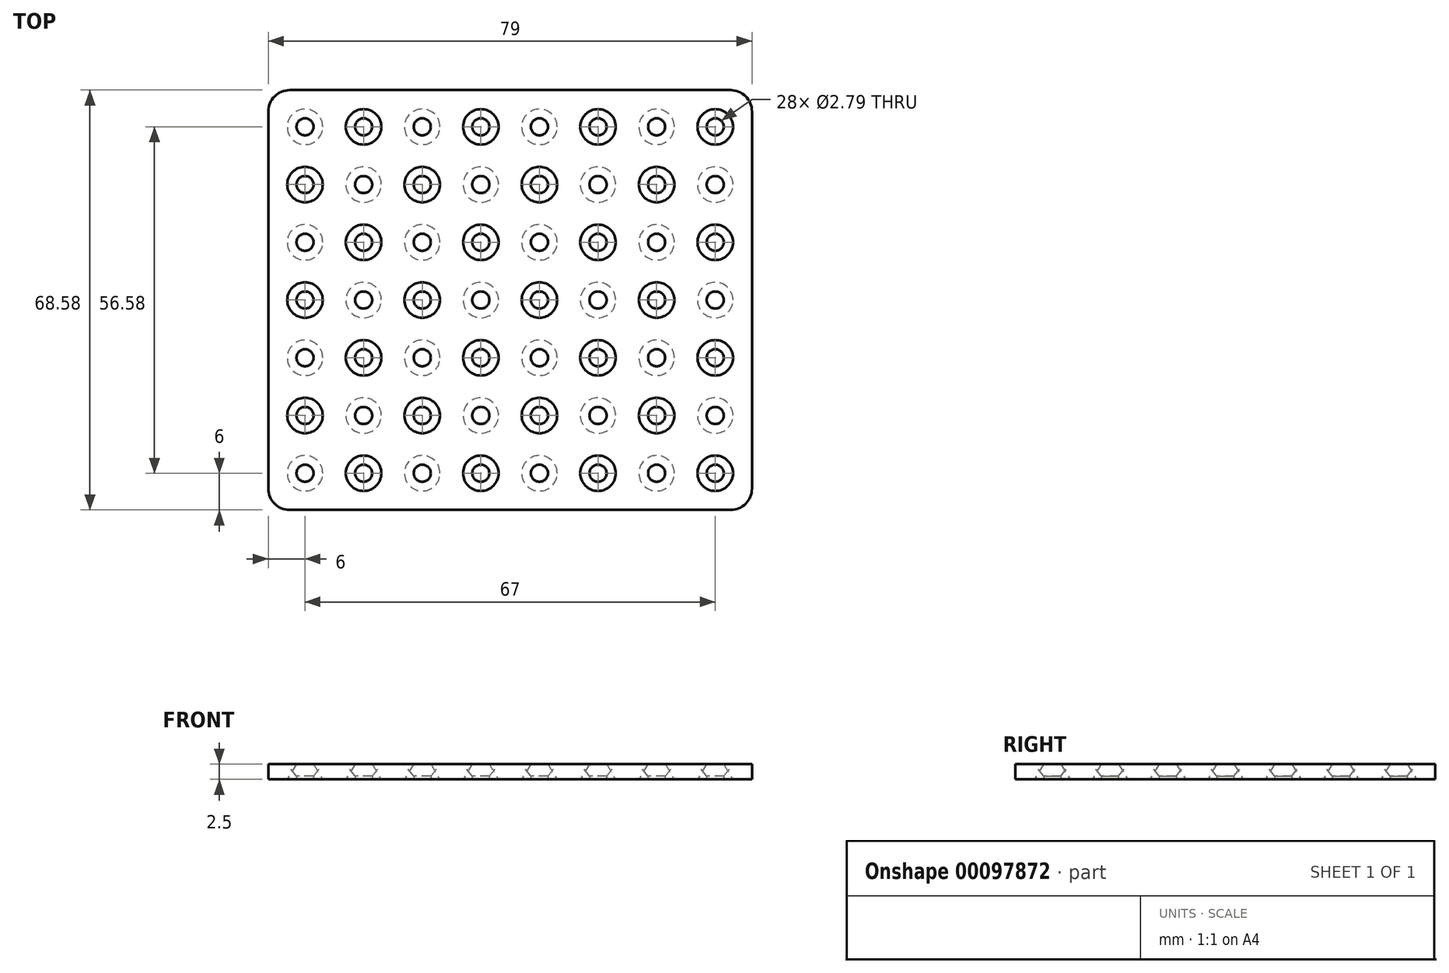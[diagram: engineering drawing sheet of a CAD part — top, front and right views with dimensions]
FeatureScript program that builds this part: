
annotation { "Feature Type Name" : "Feature", "Feature Type Description" : "" }
export const myFeature = defineFeature(function(context is Context, id is Id, definition is map)
    precondition{}
    {
        {
            var Q0;
            Q0=qCreatedBy(makeId("Top.planeOp"),FACE);
            var sketch = newSketch(context, id + "F0", { "sketchPlane" : qUnion([Q0])});
            skLineSegment(sketch, "E0.rect.bottom", {"start": v(39.5, 34.3) * mm, "end": v(-39.5, 34.3) * mm});
            skLineSegment(sketch, "E0.rect.top", {"start": v(39.5, -34.3) * mm, "end": v(-39.5, -34.3) * mm});
            skLineSegment(sketch, "E0.rect.left", {"start": v(39.5, 34.3) * mm, "end": v(39.5, -34.3) * mm});
            skLineSegment(sketch, "E0.rect.right", {"start": v(-39.5, 34.3) * mm, "end": v(-39.5, -34.3) * mm});
            skPoint(sketch, "E0.rect.middle", {"position": v(0, 0) * mm});
            skCircle(sketch, "E1", {"center": v(33.5, 28.3) * mm, "radius": 1.4 * mm});
            skCircle(sketch, "E2.0.1.0", {"center": v(33.5, 18.86) * mm, "radius": 1.4 * mm});
            skCircle(sketch, "E2.0.2.0", {"center": v(33.5, 9.43) * mm, "radius": 1.4 * mm});
            skCircle(sketch, "E2.0.3.0", {"center": v(33.5, 0) * mm, "radius": 1.4 * mm});
            skCircle(sketch, "E2.0.4.0", {"center": v(33.5, -9.43) * mm, "radius": 1.4 * mm});
            skCircle(sketch, "E2.0.5.0", {"center": v(33.5, -18.86) * mm, "radius": 1.4 * mm});
            skCircle(sketch, "E2.0.6.0", {"center": v(33.5, -28.3) * mm, "radius": 1.4 * mm});
            skCircle(sketch, "E2.1.0.0", {"center": v(23.93, 28.3) * mm, "radius": 1.4 * mm});
            skCircle(sketch, "E2.1.1.0", {"center": v(23.93, 18.86) * mm, "radius": 1.4 * mm});
            skCircle(sketch, "E2.1.2.0", {"center": v(23.93, 9.43) * mm, "radius": 1.4 * mm});
            skCircle(sketch, "E2.1.3.0", {"center": v(23.93, 0) * mm, "radius": 1.4 * mm});
            skCircle(sketch, "E2.1.4.0", {"center": v(23.93, -9.43) * mm, "radius": 1.4 * mm});
            skCircle(sketch, "E2.1.5.0", {"center": v(23.93, -18.86) * mm, "radius": 1.4 * mm});
            skCircle(sketch, "E2.1.6.0", {"center": v(23.93, -28.3) * mm, "radius": 1.4 * mm});
            skCircle(sketch, "E2.2.0.0", {"center": v(14.36, 28.3) * mm, "radius": 1.4 * mm});
            skCircle(sketch, "E2.2.1.0", {"center": v(14.36, 18.86) * mm, "radius": 1.4 * mm});
            skCircle(sketch, "E2.2.2.0", {"center": v(14.36, 9.43) * mm, "radius": 1.4 * mm});
            skCircle(sketch, "E2.2.3.0", {"center": v(14.36, 0) * mm, "radius": 1.4 * mm});
            skCircle(sketch, "E2.2.4.0", {"center": v(14.36, -9.43) * mm, "radius": 1.4 * mm});
            skCircle(sketch, "E2.2.5.0", {"center": v(14.36, -18.86) * mm, "radius": 1.4 * mm});
            skCircle(sketch, "E2.2.6.0", {"center": v(14.36, -28.3) * mm, "radius": 1.4 * mm});
            skCircle(sketch, "E2.3.0.0", {"center": v(4.79, 28.3) * mm, "radius": 1.4 * mm});
            skCircle(sketch, "E2.3.1.0", {"center": v(4.79, 18.86) * mm, "radius": 1.4 * mm});
            skCircle(sketch, "E2.3.2.0", {"center": v(4.79, 9.43) * mm, "radius": 1.4 * mm});
            skCircle(sketch, "E2.3.3.0", {"center": v(4.79, 0) * mm, "radius": 1.4 * mm});
            skCircle(sketch, "E2.3.4.0", {"center": v(4.79, -9.43) * mm, "radius": 1.4 * mm});
            skCircle(sketch, "E2.3.5.0", {"center": v(4.79, -18.86) * mm, "radius": 1.4 * mm});
            skCircle(sketch, "E2.3.6.0", {"center": v(4.79, -28.3) * mm, "radius": 1.4 * mm});
            skCircle(sketch, "E2.4.0.0", {"center": v(-4.79, 28.3) * mm, "radius": 1.4 * mm});
            skCircle(sketch, "E2.4.1.0", {"center": v(-4.79, 18.86) * mm, "radius": 1.4 * mm});
            skCircle(sketch, "E2.4.2.0", {"center": v(-4.79, 9.43) * mm, "radius": 1.4 * mm});
            skCircle(sketch, "E2.4.3.0", {"center": v(-4.79, 0) * mm, "radius": 1.4 * mm});
            skCircle(sketch, "E2.4.4.0", {"center": v(-4.79, -9.43) * mm, "radius": 1.4 * mm});
            skCircle(sketch, "E2.4.5.0", {"center": v(-4.79, -18.86) * mm, "radius": 1.4 * mm});
            skCircle(sketch, "E2.4.6.0", {"center": v(-4.79, -28.3) * mm, "radius": 1.4 * mm});
            skCircle(sketch, "E2.5.0.0", {"center": v(-14.36, 28.3) * mm, "radius": 1.4 * mm});
            skCircle(sketch, "E2.5.1.0", {"center": v(-14.36, 18.86) * mm, "radius": 1.4 * mm});
            skCircle(sketch, "E2.5.2.0", {"center": v(-14.36, 9.43) * mm, "radius": 1.4 * mm});
            skCircle(sketch, "E2.5.3.0", {"center": v(-14.36, 0) * mm, "radius": 1.4 * mm});
            skCircle(sketch, "E2.5.4.0", {"center": v(-14.36, -9.43) * mm, "radius": 1.4 * mm});
            skCircle(sketch, "E2.5.5.0", {"center": v(-14.36, -18.86) * mm, "radius": 1.4 * mm});
            skCircle(sketch, "E2.5.6.0", {"center": v(-14.36, -28.3) * mm, "radius": 1.4 * mm});
            skCircle(sketch, "E2.6.0.0", {"center": v(-23.93, 28.3) * mm, "radius": 1.4 * mm});
            skCircle(sketch, "E2.6.1.0", {"center": v(-23.93, 18.86) * mm, "radius": 1.4 * mm});
            skCircle(sketch, "E2.6.2.0", {"center": v(-23.93, 9.43) * mm, "radius": 1.4 * mm});
            skCircle(sketch, "E2.6.3.0", {"center": v(-23.93, 0) * mm, "radius": 1.4 * mm});
            skCircle(sketch, "E2.6.4.0", {"center": v(-23.93, -9.43) * mm, "radius": 1.4 * mm});
            skCircle(sketch, "E2.6.5.0", {"center": v(-23.93, -18.86) * mm, "radius": 1.4 * mm});
            skCircle(sketch, "E2.6.6.0", {"center": v(-23.93, -28.3) * mm, "radius": 1.4 * mm});
            skLineSegment(sketch, "E2.direction1", {"start": v(33.5, 28.3) * mm, "end": v(23.93, 28.3) * mm, "construction": true});
            skLineSegment(sketch, "E2.direction2", {"start": v(33.5, 28.3) * mm, "end": v(33.5, 18.86) * mm, "construction": true});
            skCircle(sketch, "E3.0.7.0", {"center": v(-33.5, 28.3) * mm, "radius": 1.4 * mm});
            skCircle(sketch, "E3.0.7.1", {"center": v(-33.5, 18.86) * mm, "radius": 1.4 * mm});
            skCircle(sketch, "E3.0.7.2", {"center": v(-33.5, 9.43) * mm, "radius": 1.4 * mm});
            skCircle(sketch, "E3.0.7.3", {"center": v(-33.5, 0) * mm, "radius": 1.4 * mm});
            skCircle(sketch, "E3.0.7.4", {"center": v(-33.5, -9.43) * mm, "radius": 1.4 * mm});
            skCircle(sketch, "E3.0.7.5", {"center": v(-33.5, -18.86) * mm, "radius": 1.4 * mm});
            skCircle(sketch, "E3.0.7.6", {"center": v(-33.5, -28.3) * mm, "radius": 1.4 * mm});
            skSolve(sketch);
        }
        {
            var Q0;
            Q0=makeQuery(id+"F0.imprint","IMPRINT",FACE,{"disambiguationData":[TD([[makeQuery(id+"F0.imprint","IMPRINT",EDGE,{"derivedFrom":sQuery(id+"F0.wireOp",EDGE,"E0.rect.bottom")}),1.0]])]});
            extrude(context, id + "F1", {"entities" : qUnion([Q0]), "endBound" : BoundingType.SYMMETRIC, "depth" : 2.5 * mm});
        }
        {
            var Q0;
            Q0=makeQuery(id+"F1.opExtrude","SWEPT_EDGE",EDGE,{"disambiguationData":[OSD([sQuery(id+"F0.wireOp",EDGE,"E0.rect.top"),sQuery(id+"F0.wireOp",EDGE,"E0.rect.left")])]});
            var Q1;
            Q1=makeQuery(id+"F1.opExtrude","SWEPT_EDGE",EDGE,{"disambiguationData":[OSD([sQuery(id+"F0.wireOp",EDGE,"E0.rect.top"),sQuery(id+"F0.wireOp",EDGE,"E0.rect.right")])]});
            var Q2;
            Q2=makeQuery(id+"F1.opExtrude","SWEPT_EDGE",EDGE,{"disambiguationData":[OSD([sQuery(id+"F0.wireOp",EDGE,"E0.rect.bottom"),sQuery(id+"F0.wireOp",EDGE,"E0.rect.right")])]});
            var Q3;
            Q3=makeQuery(id+"F1.opExtrude","SWEPT_EDGE",EDGE,{"disambiguationData":[OSD([sQuery(id+"F0.wireOp",EDGE,"E0.rect.bottom"),sQuery(id+"F0.wireOp",EDGE,"E0.rect.left")])]});
            fillet(context, id + "F2", {"entities" : qUnion([Q0, Q1, Q2, Q3]), "radius" : 3.5 * mm, "tangentPropagation" : true, "allowEdgeOverflow" : false});
        }
        {
            var Q0;
            Q0=makeQuery(id+"F1.opExtrude","CAP_EDGE",EDGE,{"disambiguationData":[OSD([sQuery(id+"F0.wireOp",EDGE,"E2.5.0.0")])],"isStart":true});
            var Q1;
            Q1=makeQuery(id+"F1.opExtrude","CAP_EDGE",EDGE,{"disambiguationData":[OSD([sQuery(id+"F0.wireOp",EDGE,"E2.6.1.0")])],"isStart":true});
            var Q2;
            Q2=makeQuery(id+"F1.opExtrude","CAP_EDGE",EDGE,{"disambiguationData":[OSD([sQuery(id+"F0.wireOp",EDGE,"E3.0.7.2")])],"isStart":true});
            var Q3;
            Q3=makeQuery(id+"F1.opExtrude","CAP_EDGE",EDGE,{"disambiguationData":[OSD([sQuery(id+"F0.wireOp",EDGE,"E2.3.0.0")])],"isStart":true});
            var Q4;
            Q4=makeQuery(id+"F1.opExtrude","CAP_EDGE",EDGE,{"disambiguationData":[OSD([sQuery(id+"F0.wireOp",EDGE,"E2.4.1.0")])],"isStart":true});
            var Q5;
            Q5=makeQuery(id+"F1.opExtrude","CAP_EDGE",EDGE,{"disambiguationData":[OSD([sQuery(id+"F0.wireOp",EDGE,"E2.5.2.0")])],"isStart":true});
            var Q6;
            Q6=makeQuery(id+"F1.opExtrude","CAP_EDGE",EDGE,{"disambiguationData":[OSD([sQuery(id+"F0.wireOp",EDGE,"E2.6.3.0")])],"isStart":true});
            var Q7;
            Q7=makeQuery(id+"F1.opExtrude","CAP_EDGE",EDGE,{"disambiguationData":[OSD([sQuery(id+"F0.wireOp",EDGE,"E3.0.7.4")])],"isStart":true});
            var Q8;
            Q8=makeQuery(id+"F1.opExtrude","CAP_EDGE",EDGE,{"disambiguationData":[OSD([sQuery(id+"F0.wireOp",EDGE,"E3.0.7.6")])],"isStart":true});
            var Q9;
            Q9=makeQuery(id+"F1.opExtrude","CAP_EDGE",EDGE,{"disambiguationData":[OSD([sQuery(id+"F0.wireOp",EDGE,"E2.6.5.0")])],"isStart":true});
            var Q10;
            Q10=makeQuery(id+"F1.opExtrude","CAP_EDGE",EDGE,{"disambiguationData":[OSD([sQuery(id+"F0.wireOp",EDGE,"E2.5.4.0")])],"isStart":true});
            var Q11;
            Q11=makeQuery(id+"F1.opExtrude","CAP_EDGE",EDGE,{"disambiguationData":[OSD([sQuery(id+"F0.wireOp",EDGE,"E2.4.3.0")])],"isStart":true});
            var Q12;
            Q12=makeQuery(id+"F1.opExtrude","CAP_EDGE",EDGE,{"disambiguationData":[OSD([sQuery(id+"F0.wireOp",EDGE,"E2.3.2.0")])],"isStart":true});
            var Q13;
            Q13=makeQuery(id+"F1.opExtrude","CAP_EDGE",EDGE,{"disambiguationData":[OSD([sQuery(id+"F0.wireOp",EDGE,"E2.2.1.0")])],"isStart":true});
            var Q14;
            Q14=makeQuery(id+"F1.opExtrude","CAP_EDGE",EDGE,{"disambiguationData":[OSD([sQuery(id+"F0.wireOp",EDGE,"E2.1.0.0")])],"isStart":true});
            var Q15;
            Q15=makeQuery(id+"F1.opExtrude","CAP_EDGE",EDGE,{"disambiguationData":[OSD([sQuery(id+"F0.wireOp",EDGE,"E2.0.1.0")])],"isStart":true});
            var Q16;
            Q16=makeQuery(id+"F1.opExtrude","CAP_EDGE",EDGE,{"disambiguationData":[OSD([sQuery(id+"F0.wireOp",EDGE,"E2.2.3.0")])],"isStart":true});
            var Q17;
            Q17=makeQuery(id+"F1.opExtrude","CAP_EDGE",EDGE,{"disambiguationData":[OSD([sQuery(id+"F0.wireOp",EDGE,"E2.3.4.0")])],"isStart":true});
            var Q18;
            Q18=makeQuery(id+"F1.opExtrude","CAP_EDGE",EDGE,{"disambiguationData":[OSD([sQuery(id+"F0.wireOp",EDGE,"E2.4.5.0")])],"isStart":true});
            var Q19;
            Q19=makeQuery(id+"F1.opExtrude","CAP_EDGE",EDGE,{"disambiguationData":[OSD([sQuery(id+"F0.wireOp",EDGE,"E2.5.6.0")])],"isStart":true});
            var Q20;
            Q20=makeQuery(id+"F1.opExtrude","CAP_EDGE",EDGE,{"disambiguationData":[OSD([sQuery(id+"F0.wireOp",EDGE,"E2.0.3.0")])],"isStart":true});
            var Q21;
            Q21=makeQuery(id+"F1.opExtrude","CAP_EDGE",EDGE,{"disambiguationData":[OSD([sQuery(id+"F0.wireOp",EDGE,"E2.1.4.0")])],"isStart":true});
            var Q22;
            Q22=makeQuery(id+"F1.opExtrude","CAP_EDGE",EDGE,{"disambiguationData":[OSD([sQuery(id+"F0.wireOp",EDGE,"E2.2.5.0")])],"isStart":true});
            var Q23;
            Q23=makeQuery(id+"F1.opExtrude","CAP_EDGE",EDGE,{"disambiguationData":[OSD([sQuery(id+"F0.wireOp",EDGE,"E2.3.6.0")])],"isStart":true});
            var Q24;
            Q24=makeQuery(id+"F1.opExtrude","CAP_EDGE",EDGE,{"disambiguationData":[OSD([sQuery(id+"F0.wireOp",EDGE,"E2.0.5.0")])],"isStart":true});
            var Q25;
            Q25=makeQuery(id+"F1.opExtrude","CAP_EDGE",EDGE,{"disambiguationData":[OSD([sQuery(id+"F0.wireOp",EDGE,"E2.1.6.0")])],"isStart":true});
            var Q26;
            Q26=makeQuery(id+"F1.opExtrude","CAP_EDGE",EDGE,{"disambiguationData":[OSD([sQuery(id+"F0.wireOp",EDGE,"E2.1.2.0")])],"isStart":true});
            var Q27;
            Q27=makeQuery(id+"F1.opExtrude","CAP_EDGE",EDGE,{"disambiguationData":[OSD([sQuery(id+"F0.wireOp",EDGE,"E3.0.7.0")])],"isStart":true});
            chamfer(context, id + "F3", {"entities" : qUnion([Q0, Q1, Q2, Q3, Q4, Q5, Q6, Q7, Q8, Q9, Q10, Q11, Q12, Q13, Q14, Q15, Q16, Q17, Q18, Q19, Q20, Q21, Q22, Q23, Q24, Q25, Q26, Q27]), "chamferType" : ChamferType.TWO_OFFSETS, "width1" : 1.5 * mm, "oppositeDirection" : false, "width2" : 2.5 * mm, "tangentPropagation" : true});
        }
        {
            var Q0;
            Q0=makeQuery(id+"F1.opExtrude","CAP_EDGE",EDGE,{"disambiguationData":[OSD([sQuery(id+"F0.wireOp",EDGE,"E2.6.0.0")])],"isStart":false});
            var Q1;
            Q1=makeQuery(id+"F1.opExtrude","CAP_EDGE",EDGE,{"disambiguationData":[OSD([sQuery(id+"F0.wireOp",EDGE,"E3.0.7.3")])],"isStart":false});
            var Q2;
            Q2=makeQuery(id+"F1.opExtrude","CAP_EDGE",EDGE,{"disambiguationData":[OSD([sQuery(id+"F0.wireOp",EDGE,"E2.6.2.0")])],"isStart":false});
            var Q3;
            Q3=makeQuery(id+"F1.opExtrude","CAP_EDGE",EDGE,{"disambiguationData":[OSD([sQuery(id+"F0.wireOp",EDGE,"E2.5.1.0")])],"isStart":false});
            var Q4;
            Q4=makeQuery(id+"F1.opExtrude","CAP_EDGE",EDGE,{"disambiguationData":[OSD([sQuery(id+"F0.wireOp",EDGE,"E2.4.0.0")])],"isStart":false});
            var Q5;
            Q5=makeQuery(id+"F1.opExtrude","CAP_EDGE",EDGE,{"disambiguationData":[OSD([sQuery(id+"F0.wireOp",EDGE,"E3.0.7.5")])],"isStart":false});
            var Q6;
            Q6=makeQuery(id+"F1.opExtrude","CAP_EDGE",EDGE,{"disambiguationData":[OSD([sQuery(id+"F0.wireOp",EDGE,"E2.6.4.0")])],"isStart":false});
            var Q7;
            Q7=makeQuery(id+"F1.opExtrude","CAP_EDGE",EDGE,{"disambiguationData":[OSD([sQuery(id+"F0.wireOp",EDGE,"E2.5.3.0")])],"isStart":false});
            var Q8;
            Q8=makeQuery(id+"F1.opExtrude","CAP_EDGE",EDGE,{"disambiguationData":[OSD([sQuery(id+"F0.wireOp",EDGE,"E2.4.2.0")])],"isStart":false});
            var Q9;
            Q9=makeQuery(id+"F1.opExtrude","CAP_EDGE",EDGE,{"disambiguationData":[OSD([sQuery(id+"F0.wireOp",EDGE,"E2.3.1.0")])],"isStart":false});
            var Q10;
            Q10=makeQuery(id+"F1.opExtrude","CAP_EDGE",EDGE,{"disambiguationData":[OSD([sQuery(id+"F0.wireOp",EDGE,"E2.2.0.0")])],"isStart":false});
            var Q11;
            Q11=makeQuery(id+"F1.opExtrude","CAP_EDGE",EDGE,{"disambiguationData":[OSD([sQuery(id+"F0.wireOp",EDGE,"E2.1.1.0")])],"isStart":false});
            var Q12;
            Q12=makeQuery(id+"F1.opExtrude","CAP_EDGE",EDGE,{"disambiguationData":[OSD([sQuery(id+"F0.wireOp",EDGE,"E1")])],"isStart":false});
            var Q13;
            Q13=makeQuery(id+"F1.opExtrude","CAP_EDGE",EDGE,{"disambiguationData":[OSD([sQuery(id+"F0.wireOp",EDGE,"E2.2.2.0")])],"isStart":false});
            var Q14;
            Q14=makeQuery(id+"F1.opExtrude","CAP_EDGE",EDGE,{"disambiguationData":[OSD([sQuery(id+"F0.wireOp",EDGE,"E2.3.3.0")])],"isStart":false});
            var Q15;
            Q15=makeQuery(id+"F1.opExtrude","CAP_EDGE",EDGE,{"disambiguationData":[OSD([sQuery(id+"F0.wireOp",EDGE,"E2.4.4.0")])],"isStart":false});
            var Q16;
            Q16=makeQuery(id+"F1.opExtrude","CAP_EDGE",EDGE,{"disambiguationData":[OSD([sQuery(id+"F0.wireOp",EDGE,"E2.5.5.0")])],"isStart":false});
            var Q17;
            Q17=makeQuery(id+"F1.opExtrude","CAP_EDGE",EDGE,{"disambiguationData":[OSD([sQuery(id+"F0.wireOp",EDGE,"E2.6.6.0")])],"isStart":false});
            var Q18;
            Q18=makeQuery(id+"F1.opExtrude","CAP_EDGE",EDGE,{"disambiguationData":[OSD([sQuery(id+"F0.wireOp",EDGE,"E2.1.3.0")])],"isStart":false});
            var Q19;
            Q19=makeQuery(id+"F1.opExtrude","CAP_EDGE",EDGE,{"disambiguationData":[OSD([sQuery(id+"F0.wireOp",EDGE,"E2.0.4.0")])],"isStart":false});
            var Q20;
            Q20=makeQuery(id+"F1.opExtrude","CAP_EDGE",EDGE,{"disambiguationData":[OSD([sQuery(id+"F0.wireOp",EDGE,"E2.0.2.0")])],"isStart":false});
            var Q21;
            Q21=makeQuery(id+"F1.opExtrude","CAP_EDGE",EDGE,{"disambiguationData":[OSD([sQuery(id+"F0.wireOp",EDGE,"E2.2.4.0")])],"isStart":false});
            var Q22;
            Q22=makeQuery(id+"F1.opExtrude","CAP_EDGE",EDGE,{"disambiguationData":[OSD([sQuery(id+"F0.wireOp",EDGE,"E2.1.5.0")])],"isStart":false});
            var Q23;
            Q23=makeQuery(id+"F1.opExtrude","CAP_EDGE",EDGE,{"disambiguationData":[OSD([sQuery(id+"F0.wireOp",EDGE,"E2.0.6.0")])],"isStart":false});
            var Q24;
            Q24=makeQuery(id+"F1.opExtrude","CAP_EDGE",EDGE,{"disambiguationData":[OSD([sQuery(id+"F0.wireOp",EDGE,"E2.3.5.0")])],"isStart":false});
            var Q25;
            Q25=makeQuery(id+"F1.opExtrude","CAP_EDGE",EDGE,{"disambiguationData":[OSD([sQuery(id+"F0.wireOp",EDGE,"E2.2.6.0")])],"isStart":false});
            var Q26;
            Q26=makeQuery(id+"F1.opExtrude","CAP_EDGE",EDGE,{"disambiguationData":[OSD([sQuery(id+"F0.wireOp",EDGE,"E2.4.6.0")])],"isStart":false});
            var Q27;
            Q27=makeQuery(id+"F1.opExtrude","CAP_EDGE",EDGE,{"disambiguationData":[OSD([sQuery(id+"F0.wireOp",EDGE,"E3.0.7.1")])],"isStart":false});
            chamfer(context, id + "F4", {"entities" : qUnion([Q0, Q1, Q2, Q3, Q4, Q5, Q6, Q7, Q8, Q9, Q10, Q11, Q12, Q13, Q14, Q15, Q16, Q17, Q18, Q19, Q20, Q21, Q22, Q23, Q24, Q25, Q26, Q27]), "chamferType" : ChamferType.TWO_OFFSETS, "width1" : 2 * mm, "oppositeDirection" : false, "width2" : 1.5 * mm, "tangentPropagation" : true});
        }
    });
